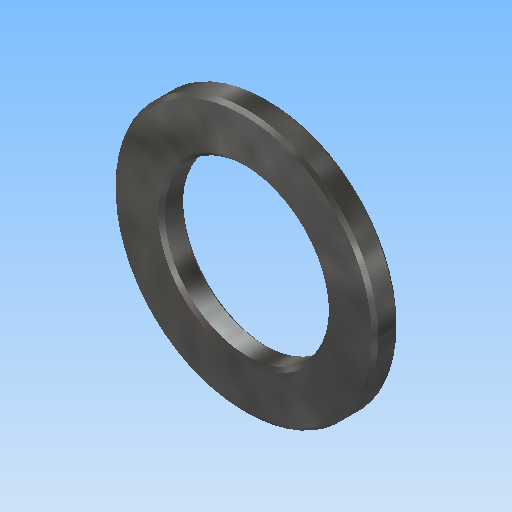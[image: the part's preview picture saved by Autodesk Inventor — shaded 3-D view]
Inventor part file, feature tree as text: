
AUTODESK INVENTOR PART (.ipt)
format: ipt  version: 2018 (Build 220112000, 112)  size: 138,752 bytes
history: native  units: mm
features: extrude x1, chamfer x1, sketch x1
ambient origin geometry x8: Origin, YZ Plane, XZ Plane, XY Plane, X Axis, Y Axis, Z Axis, Center Point
bodies: Solid1 (feature_tree)
feature tree (3):
  extrude  "Extrusion1"  Depth=1.5mm
  chamfer  "Chamfer1"  Distance=1.5mm
  sketch  "Sketch1"  dims[d0=10.0mm d1=16.0mm d2=1.5mm d3=0.0mm d4=0.2mm d5=2.0mm d6=45.0deg]
